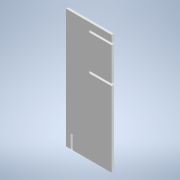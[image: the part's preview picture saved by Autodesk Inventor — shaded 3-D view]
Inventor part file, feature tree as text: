
AUTODESK INVENTOR PART (.ipt)
format: ipt  version: 2020 (Build 240168000, 168)  size: 174,592 bytes
history: native  units: in
note: dims shown in document units (in); Inventor stores cm internally (conversion verified against a paired STEP export)
features: extrude x1
ambient origin geometry x8: Origin, YZ Plane, XZ Plane, XY Plane, X Axis, Y Axis, Z Axis, Center Point
bodies: Solid1 (feature_tree)
feature tree (1):
  extrude  "Extrusion1"  Depth=0.23in
